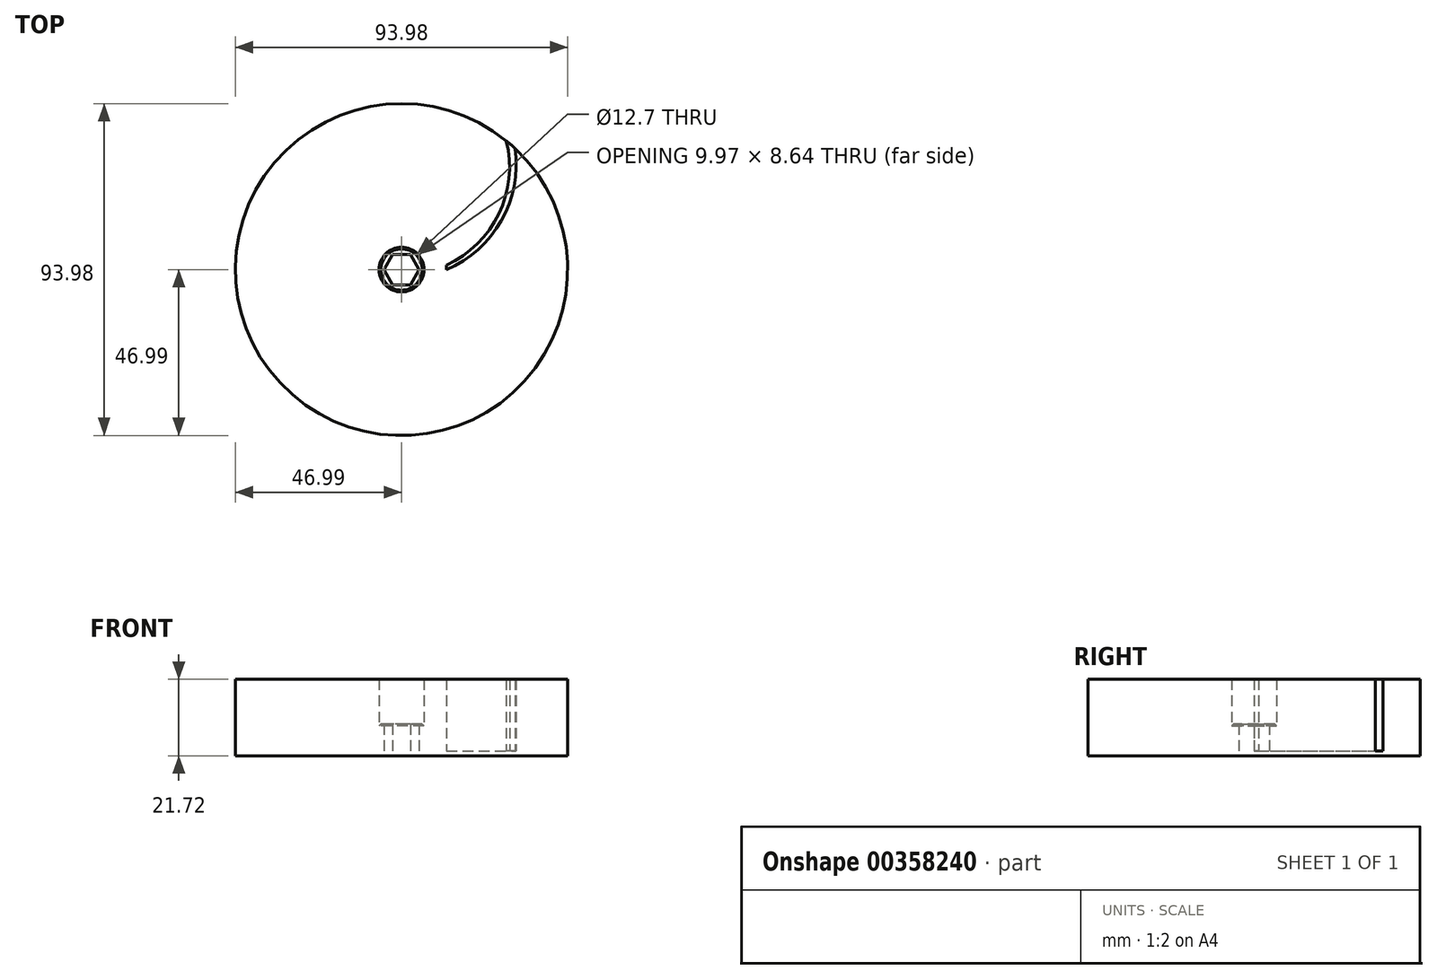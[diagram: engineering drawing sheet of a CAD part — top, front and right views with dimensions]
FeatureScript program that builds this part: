
annotation { "Feature Type Name" : "Feature", "Feature Type Description" : "" }
export const myFeature = defineFeature(function(context is Context, id is Id, definition is map)
    precondition{}
    {
        {
            var Q0;
            Q0=qCreatedBy(makeId("Top.planeOp"),FACE);
            var sketch = newSketch(context, id + "F0", { "sketchPlane" : qUnion([Q0])});
            skCircle(sketch, "E0", {"center": v(0, 0) * mm, "radius": 47 * mm});
            skSolve(sketch);
        }
        {
            var Q0;
            Q0=makeQuery(id+"F0.imprint","IMPRINT",FACE,{"disambiguationData":[TD([[makeQuery(id+"F0.imprint","IMPRINT",EDGE,{"derivedFrom":sQuery(id+"F0.wireOp",EDGE,"E0")}),1.0]])]});
            extrude(context, id + "F1", {"entities" : qUnion([Q0]), "depth" : 1.4 * mm});
        }
        {
            var Q0;
            Q0=makeQuery(id+"F1.opExtrude","CAP_FACE",FACE,{"disambiguationData":[OSD([sQuery(id+"F0.wireOp",EDGE,"E0")])],"isStart":true});
            var sketch = newSketch(context, id + "F2", { "sketchPlane" : qUnion([Q0])});
            skCircle(sketch, "E1.cCircle", {"center": v(0, 0) * mm, "radius": 4.32 * mm, "construction": true});
            skLineSegment(sketch, "E1.0", {"start": v(-2.5, 4.32) * mm, "end": v(2.5, 4.32) * mm});
            skLineSegment(sketch, "E1.1", {"start": v(2.5, 4.32) * mm, "end": v(4.99, 0) * mm});
            skLineSegment(sketch, "E1.2", {"start": v(4.99, 0) * mm, "end": v(2.5, -4.32) * mm});
            skLineSegment(sketch, "E1.3", {"start": v(2.5, -4.32) * mm, "end": v(-2.5, -4.32) * mm});
            skLineSegment(sketch, "E1.4", {"start": v(-2.5, -4.32) * mm, "end": v(-4.99, 0) * mm});
            skLineSegment(sketch, "E1.5", {"start": v(-4.99, 0) * mm, "end": v(-2.5, 4.32) * mm});
            skPoint(sketch, "E1.0.midPoint", {"position": v(0, 4.32) * mm});
            skSolve(sketch);
        }
        {
            var Q0;
            Q0=makeQuery(id+"F2.imprint","IMPRINT",FACE,{"disambiguationData":[TD([[makeQuery(id+"F2.imprint","IMPRINT",EDGE,{"derivedFrom":sQuery(id+"F2.wireOp",EDGE,"E1.0")}),-1.0]])]});
            extrude(context, id + "F3", {"entities" : qUnion([Q0]), "operationType" : NewBodyOperationType.REMOVE, "oppositeDirection" : true, "depth" : 25.4 * mm});
        }
        {
            var Q0;
            Q0=makeQuery(id+"F1.opExtrude","CAP_FACE",FACE,{"disambiguationData":[OSD([sQuery(id+"F0.wireOp",EDGE,"E0")])],"isStart":false});
            var sketch = newSketch(context, id + "F4", { "sketchPlane" : qUnion([Q0])});
            skCircle(sketch, "E2", {"center": v(0, 0) * mm, "radius": 6.35 * mm});
            skSolve(sketch);
        }
        {
            var Q0;
            Q0=makeQuery(id+"F4.imprint","IMPRINT",FACE,{"disambiguationData":[TD([[makeQuery(id+"F4.imprint","IMPRINT",EDGE,{"derivedFrom":sQuery(id+"F4.wireOp",EDGE,"E2")}),1.0]])]});
            extrude(context, id + "F5", {"entities" : qUnion([Q0]), "operationType" : NewBodyOperationType.ADD, "depth" : 7.62 * mm});
        }
        {
            var Q0;
            Q0=makeQuery(id+"F5.opExtrude","CAP_EDGE",EDGE,{"disambiguationData":[OSD([sQuery(id+"F4.wireOp",EDGE,"E2")])],"isStart":false});
            chamfer(context, id + "F6", {"entities" : qUnion([Q0]), "width" : 0.5 * mm, "tangentPropagation" : true});
        }
        {
            var Q0;
            Q0=makeQuery(id+"F1.opExtrude","CAP_FACE",FACE,{"disambiguationData":[OSD([sQuery(id+"F0.wireOp",EDGE,"E0")])],"isStart":false});
            var sketch = newSketch(context, id + "F7", { "sketchPlane" : qUnion([Q0])});
            skCircle(sketch, "E3", {"center": v(0, 0) * mm, "radius": 12.7 * mm, "construction": true});
            skArc(sketch, "E4", {"start": v(32.13, 34.3) * mm, "mid": v(28.22, 13.86) * mm, "end": v(12.7, 0) * mm});
            skLineSegment(sketch, "E5", {"start": v(0, 12.7) * mm, "end": v(0, 47) * mm, "construction": true});
            skArc(sketch, "E6", {"start": v(12.64, 1.27) * mm, "mid": v(27.5, 15.79) * mm, "end": v(29.65, 36.46) * mm});
            skLineSegment(sketch, "E7", {"start": v(12.64, 1.27) * mm, "end": v(12.7, 0) * mm});
            skArc(sketch, "E8.1.0", {"start": v(10.3, 7.42) * mm, "mid": v(15.93, 27.43) * mm, "end": v(7.44, 46.4) * mm});
            skArc(sketch, "E8.1.1", {"start": v(10.68, 45.76) * mm, "mid": v(17.51, 26.1) * mm, "end": v(11, 6.35) * mm});
            skLineSegment(sketch, "E8.1.2", {"start": v(10.3, 7.42) * mm, "end": v(11, 6.35) * mm});
            skArc(sketch, "E8.2.0", {"start": v(5.22, 11.58) * mm, "mid": v(0.08, 31.71) * mm, "end": v(-16.75, 43.9) * mm});
            skArc(sketch, "E8.2.1", {"start": v(-13.63, 44.97) * mm, "mid": v(2.11, 31.37) * mm, "end": v(6.35, 11) * mm});
            skLineSegment(sketch, "E8.2.2", {"start": v(5.22, 11.58) * mm, "end": v(6.35, 11) * mm});
            skArc(sketch, "E8.3.0", {"start": v(-1.27, 12.64) * mm, "mid": v(-15.79, 27.5) * mm, "end": v(-36.46, 29.65) * mm});
            skArc(sketch, "E8.3.1", {"start": v(-34.3, 32.13) * mm, "mid": v(-13.86, 28.22) * mm, "end": v(0, 12.7) * mm});
            skLineSegment(sketch, "E8.3.2", {"start": v(-1.27, 12.64) * mm, "end": v(0, 12.7) * mm});
            skArc(sketch, "E8.4.0", {"start": v(-7.42, 10.3) * mm, "mid": v(-27.43, 15.93) * mm, "end": v(-46.4, 7.44) * mm});
            skArc(sketch, "E8.4.1", {"start": v(-45.76, 10.68) * mm, "mid": v(-26.1, 17.51) * mm, "end": v(-6.35, 11) * mm});
            skLineSegment(sketch, "E8.4.2", {"start": v(-7.42, 10.3) * mm, "end": v(-6.35, 11) * mm});
            skArc(sketch, "E8.5.0", {"start": v(-11.58, 5.22) * mm, "mid": v(-31.71, 0.08) * mm, "end": v(-43.9, -16.75) * mm});
            skArc(sketch, "E8.5.1", {"start": v(-44.97, -13.63) * mm, "mid": v(-31.37, 2.11) * mm, "end": v(-11, 6.35) * mm});
            skLineSegment(sketch, "E8.5.2", {"start": v(-11.58, 5.22) * mm, "end": v(-11, 6.35) * mm});
            skArc(sketch, "E8.6.0", {"start": v(-12.64, -1.27) * mm, "mid": v(-27.5, -15.79) * mm, "end": v(-29.65, -36.46) * mm});
            skArc(sketch, "E8.6.1", {"start": v(-32.13, -34.3) * mm, "mid": v(-28.22, -13.86) * mm, "end": v(-12.7, 0) * mm});
            skLineSegment(sketch, "E8.6.2", {"start": v(-12.64, -1.27) * mm, "end": v(-12.7, 0) * mm});
            skArc(sketch, "E8.7.0", {"start": v(-10.3, -7.42) * mm, "mid": v(-15.93, -27.43) * mm, "end": v(-7.44, -46.4) * mm});
            skArc(sketch, "E8.7.1", {"start": v(-10.68, -45.76) * mm, "mid": v(-17.51, -26.1) * mm, "end": v(-11, -6.35) * mm});
            skLineSegment(sketch, "E8.7.2", {"start": v(-10.3, -7.42) * mm, "end": v(-11, -6.35) * mm});
            skArc(sketch, "E8.8.0", {"start": v(-5.22, -11.58) * mm, "mid": v(-0.08, -31.71) * mm, "end": v(16.75, -43.9) * mm});
            skArc(sketch, "E8.8.1", {"start": v(13.63, -44.97) * mm, "mid": v(-2.11, -31.37) * mm, "end": v(-6.35, -11) * mm});
            skLineSegment(sketch, "E8.8.2", {"start": v(-5.22, -11.58) * mm, "end": v(-6.35, -11) * mm});
            skArc(sketch, "E8.9.0", {"start": v(1.27, -12.64) * mm, "mid": v(15.79, -27.5) * mm, "end": v(36.46, -29.65) * mm});
            skArc(sketch, "E8.9.1", {"start": v(34.3, -32.13) * mm, "mid": v(13.86, -28.22) * mm, "end": v(0, -12.7) * mm});
            skLineSegment(sketch, "E8.9.2", {"start": v(1.27, -12.64) * mm, "end": v(0, -12.7) * mm});
            skArc(sketch, "E8.10.0", {"start": v(7.42, -10.3) * mm, "mid": v(27.43, -15.93) * mm, "end": v(46.4, -7.44) * mm});
            skArc(sketch, "E8.10.1", {"start": v(45.76, -10.68) * mm, "mid": v(26.1, -17.51) * mm, "end": v(6.35, -11) * mm});
            skLineSegment(sketch, "E8.10.2", {"start": v(7.42, -10.3) * mm, "end": v(6.35, -11) * mm});
            skArc(sketch, "E8.11.0", {"start": v(11.58, -5.22) * mm, "mid": v(31.71, -0.08) * mm, "end": v(43.9, 16.75) * mm});
            skArc(sketch, "E8.11.1", {"start": v(44.97, 13.63) * mm, "mid": v(31.37, -2.11) * mm, "end": v(11, -6.35) * mm});
            skLineSegment(sketch, "E8.11.2", {"start": v(11.58, -5.22) * mm, "end": v(11, -6.35) * mm});
            skSolve(sketch);
        }
        {
            var Q0;
            {var subQ0=sQuery(id+"F7.wireOp",EDGE,"E8.1.0");Q0=makeQuery(id+"F7.imprint","IMPRINT",FACE,{"disambiguationData":[TD([[makeQuery(id+"F7.imprint","IMPRINT",EDGE,{"derivedFrom":subQ0}),-1.0]])]});}
            var Q1;
            {var subQ0=sQuery(id+"F7.wireOp",EDGE,"E4");Q1=makeQuery(id+"F7.imprint","IMPRINT",FACE,{"disambiguationData":[TD([[makeQuery(id+"F7.imprint","IMPRINT",EDGE,{"derivedFrom":subQ0}),-1.0]])]});}
            var Q2;
            {var subQ0=sQuery(id+"F7.wireOp",EDGE,"E8.11.0");Q2=makeQuery(id+"F7.imprint","IMPRINT",FACE,{"disambiguationData":[TD([[makeQuery(id+"F7.imprint","IMPRINT",EDGE,{"derivedFrom":subQ0}),-1.0]])]});}
            var Q3;
            {var subQ0=sQuery(id+"F7.wireOp",EDGE,"E8.10.0");Q3=makeQuery(id+"F7.imprint","IMPRINT",FACE,{"disambiguationData":[TD([[makeQuery(id+"F7.imprint","IMPRINT",EDGE,{"derivedFrom":subQ0}),-1.0]])]});}
            var Q4;
            {var subQ0=sQuery(id+"F7.wireOp",EDGE,"E8.9.0");Q4=makeQuery(id+"F7.imprint","IMPRINT",FACE,{"disambiguationData":[TD([[makeQuery(id+"F7.imprint","IMPRINT",EDGE,{"derivedFrom":subQ0}),-1.0]])]});}
            var Q5;
            {var subQ0=sQuery(id+"F7.wireOp",EDGE,"E8.8.0");Q5=makeQuery(id+"F7.imprint","IMPRINT",FACE,{"disambiguationData":[TD([[makeQuery(id+"F7.imprint","IMPRINT",EDGE,{"derivedFrom":subQ0}),-1.0]])]});}
            var Q6;
            {var subQ0=sQuery(id+"F7.wireOp",EDGE,"E8.7.0");Q6=makeQuery(id+"F7.imprint","IMPRINT",FACE,{"disambiguationData":[TD([[makeQuery(id+"F7.imprint","IMPRINT",EDGE,{"derivedFrom":subQ0}),-1.0]])]});}
            var Q7;
            {var subQ0=sQuery(id+"F7.wireOp",EDGE,"E8.6.0");Q7=makeQuery(id+"F7.imprint","IMPRINT",FACE,{"disambiguationData":[TD([[makeQuery(id+"F7.imprint","IMPRINT",EDGE,{"derivedFrom":subQ0}),-1.0]])]});}
            var Q8;
            {var subQ0=sQuery(id+"F7.wireOp",EDGE,"E8.5.0");Q8=makeQuery(id+"F7.imprint","IMPRINT",FACE,{"disambiguationData":[TD([[makeQuery(id+"F7.imprint","IMPRINT",EDGE,{"derivedFrom":subQ0}),-1.0]])]});}
            var Q9;
            {var subQ0=sQuery(id+"F7.wireOp",EDGE,"E8.4.0");Q9=makeQuery(id+"F7.imprint","IMPRINT",FACE,{"disambiguationData":[TD([[makeQuery(id+"F7.imprint","IMPRINT",EDGE,{"derivedFrom":subQ0}),-1.0]])]});}
            var Q10;
            {var subQ0=sQuery(id+"F7.wireOp",EDGE,"E8.3.0");Q10=makeQuery(id+"F7.imprint","IMPRINT",FACE,{"disambiguationData":[TD([[makeQuery(id+"F7.imprint","IMPRINT",EDGE,{"derivedFrom":subQ0}),-1.0]])]});}
            var Q11;
            {var subQ0=sQuery(id+"F7.wireOp",EDGE,"E8.2.0");Q11=makeQuery(id+"F7.imprint","IMPRINT",FACE,{"disambiguationData":[TD([[makeQuery(id+"F7.imprint","IMPRINT",EDGE,{"derivedFrom":subQ0}),-1.0]])]});}
            extrude(context, id + "F8", {"entities" : qUnion([Q0, Q1, Q2, Q3, Q4, Q5, Q6, Q7, Q8, Q9, Q10, Q11]), "operationType" : NewBodyOperationType.ADD, "depth" : 20.32 * mm});
        }
    });
